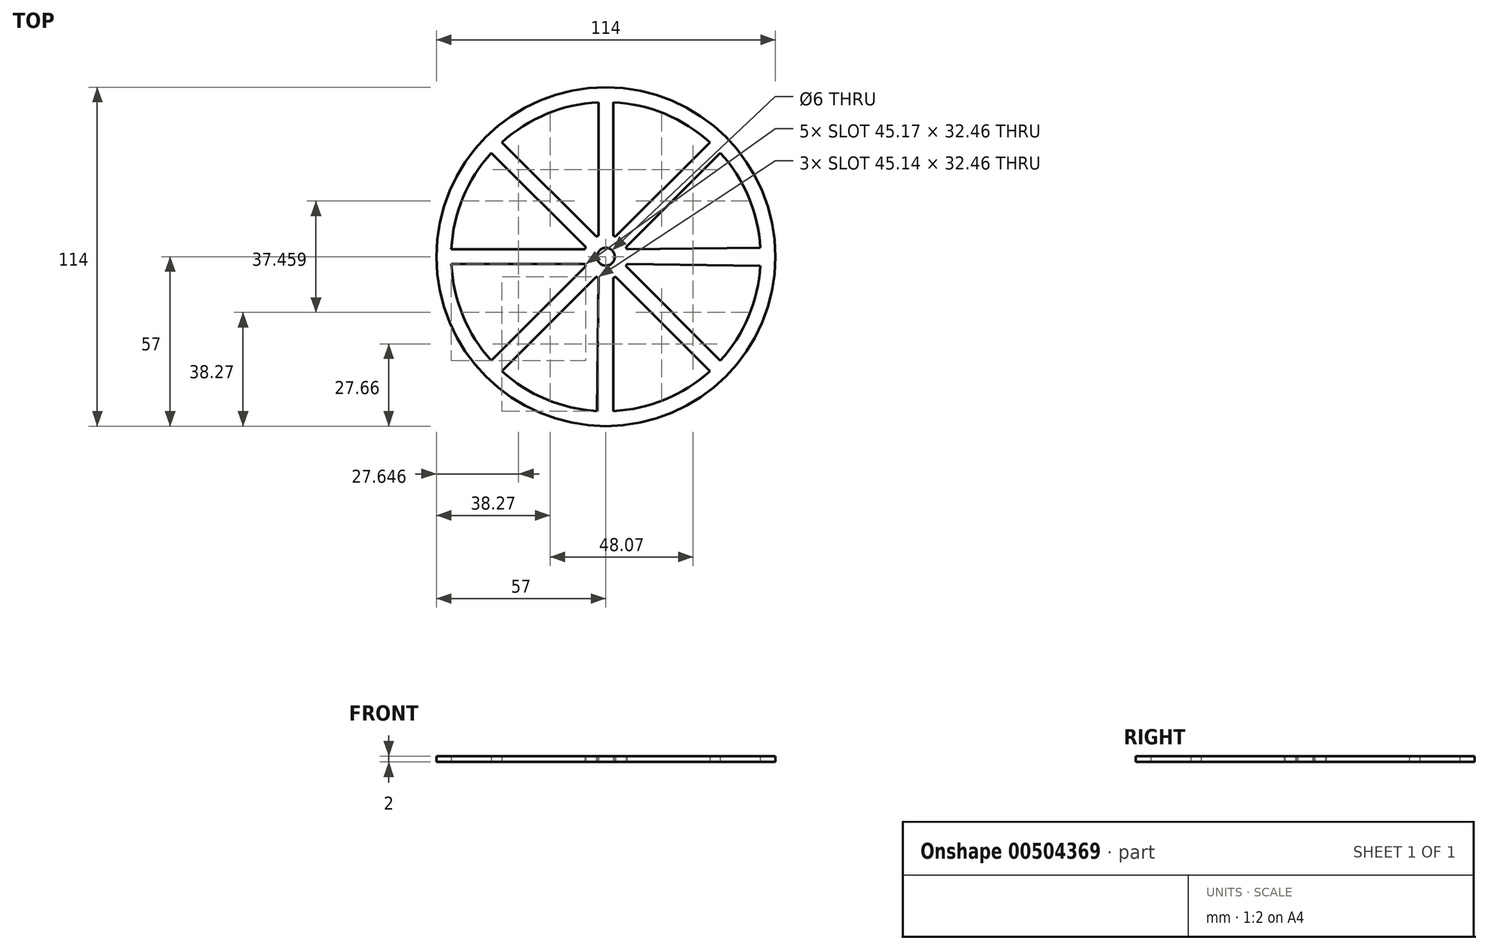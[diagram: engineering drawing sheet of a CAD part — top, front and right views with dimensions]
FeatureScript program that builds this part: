
annotation { "Feature Type Name" : "Feature", "Feature Type Description" : "" }
export const myFeature = defineFeature(function(context is Context, id is Id, definition is map)
    precondition{}
    {
        {
            var Q0;
            Q0=qCreatedBy(makeId("Top.planeOp"),FACE);
            var sketch = newSketch(context, id + "F0", { "sketchPlane" : qUnion([Q0])});
            skArc(sketch, "E0", {"start": v(-38.5, 34.96) * mm, "mid": v(-48.04, 19.9) * mm, "end": v(-51.94, 2.5) * mm});
            skCircle(sketch, "E1", {"center": v(0, 0) * mm, "radius": 57 * mm});
            skLineSegment(sketch, "E2", {"start": v(0, 0) * mm, "end": v(-34.96, 34.96) * mm, "construction": true});
            skLineSegment(sketch, "E3.left", {"start": v(-2.5, 51.94) * mm, "end": v(-2.5, 7.07) * mm});
            skLineSegment(sketch, "E3.right", {"start": v(2.5, 42.93) * mm, "end": v(2.5, 7.07) * mm});
            skLineSegment(sketch, "E4.bottom", {"start": v(-51.94, 2.5) * mm, "end": v(-7.07, 2.5) * mm});
            skLineSegment(sketch, "E4.top", {"start": v(-51.94, -2.5) * mm, "end": v(-7.07, -2.5) * mm});
            skLineSegment(sketch, "E5", {"start": v(-34.96, 38.5) * mm, "end": v(-3.23, 6.77) * mm});
            skLineSegment(sketch, "E6.MirrorCS", {"start": v(-38.5, 34.96) * mm, "end": v(-6.77, 3.23) * mm});
            skLineSegment(sketch, "E7.MirrorCS", {"start": v(34.96, 38.5) * mm, "end": v(3.23, 6.77) * mm});
            skArc(sketch, "E8", {"start": v(-2.5, 7.07) * mm, "mid": v(-2.87, 6.93) * mm, "end": v(-3.23, 6.77) * mm});
            skArc(sketch, "E9.trimOffspring", {"start": v(-6.77, 3.23) * mm, "mid": v(-6.93, 2.87) * mm, "end": v(-7.07, 2.5) * mm});
            skArc(sketch, "E10.trimOffspring", {"start": v(-7.07, -2.5) * mm, "mid": v(-6.93, -2.87) * mm, "end": v(-6.77, -3.23) * mm});
            skLineSegment(sketch, "E11.trimOffspring", {"start": v(-6.77, -3.23) * mm, "end": v(-38.5, -34.96) * mm});
            skArc(sketch, "E12.trimOffspring", {"start": v(-3.23, -6.77) * mm, "mid": v(-2.87, -6.93) * mm, "end": v(-2.5, -7.07) * mm});
            skLineSegment(sketch, "E13.trimOffspring", {"start": v(-3.23, -6.77) * mm, "end": v(-34.96, -38.5) * mm});
            skLineSegment(sketch, "E14.trimOffspring", {"start": v(-2.5, -7.07) * mm, "end": v(-3.02, -51.91) * mm});
            skLineSegment(sketch, "E15.trimOffspring", {"start": v(2.5, -7.07) * mm, "end": v(2.5, -51.94) * mm});
            skLineSegment(sketch, "E16.trimOffspring", {"start": v(3.23, -6.77) * mm, "end": v(34.96, -38.5) * mm});
            skArc(sketch, "E17.trimOffspring", {"start": v(2.5, -7.07) * mm, "mid": v(2.87, -6.93) * mm, "end": v(3.23, -6.77) * mm});
            skArc(sketch, "E18.trimOffspring", {"start": v(6.77, -3.23) * mm, "mid": v(6.93, -2.87) * mm, "end": v(7.07, -2.5) * mm});
            skLineSegment(sketch, "E19.trimOffspring", {"start": v(6.77, -3.23) * mm, "end": v(38.5, -34.96) * mm});
            skLineSegment(sketch, "E20.trimOffspring", {"start": v(7.07, -2.5) * mm, "end": v(51.91, -3.02) * mm});
            skArc(sketch, "E21.trimOffspring", {"start": v(7.07, 2.5) * mm, "mid": v(6.93, 2.87) * mm, "end": v(6.77, 3.23) * mm});
            skArc(sketch, "E22.trimOffspring", {"start": v(3.23, 6.77) * mm, "mid": v(2.87, 6.93) * mm, "end": v(2.5, 7.07) * mm});
            skLineSegment(sketch, "E23.trimOffspring", {"start": v(7.07, 2.5) * mm, "end": v(51.91, 3.02) * mm});
            skPoint(sketch, "E24.MirrorCS.start.orphan", {"position": v(38.5, 34.96) * mm});
            skCircle(sketch, "E25", {"center": v(0, 0) * mm, "radius": 3 * mm});
            skLineSegment(sketch, "E26.MirrorCS", {"start": v(38.5, 34.96) * mm, "end": v(6.77, 3.23) * mm});
            skArc(sketch, "E27.trimOffspring", {"start": v(34.96, 38.5) * mm, "mid": v(19.9, 48.04) * mm, "end": v(2.5, 51.94) * mm});
            skArc(sketch, "E28.trimOffspring", {"start": v(38.5, -34.96) * mm, "mid": v(47.94, -20.14) * mm, "end": v(51.91, -3.02) * mm});
            skArc(sketch, "E29.trimOffspring", {"start": v(-34.96, -38.5) * mm, "mid": v(-20.14, -47.94) * mm, "end": v(-3.02, -51.91) * mm});
            skArc(sketch, "E30.trimOffspring", {"start": v(2.5, -51.94) * mm, "mid": v(19.9, -48.04) * mm, "end": v(34.96, -38.5) * mm});
            skArc(sketch, "E31.trimOffspring", {"start": v(51.91, 3.02) * mm, "mid": v(47.94, 20.14) * mm, "end": v(38.5, 34.96) * mm});
            skArc(sketch, "E32.trimOffspring", {"start": v(-51.94, -2.5) * mm, "mid": v(-48.04, -19.9) * mm, "end": v(-38.5, -34.96) * mm});
            skLineSegment(sketch, "E33", {"start": v(2.5, 42.93) * mm, "end": v(2.5, 51.94) * mm});
            skArc(sketch, "E34.trimOffspring", {"start": v(-2.5, 51.94) * mm, "mid": v(-19.9, 48.04) * mm, "end": v(-34.96, 38.5) * mm});
            skSolve(sketch);
        }
        {
            var Q0;
            Q0=qSketchRegion(id+"F0",true);
            extrude(context, id + "F1", {"entities" : qUnion([Q0]), "depth" : 2 * mm});
        }
    });
